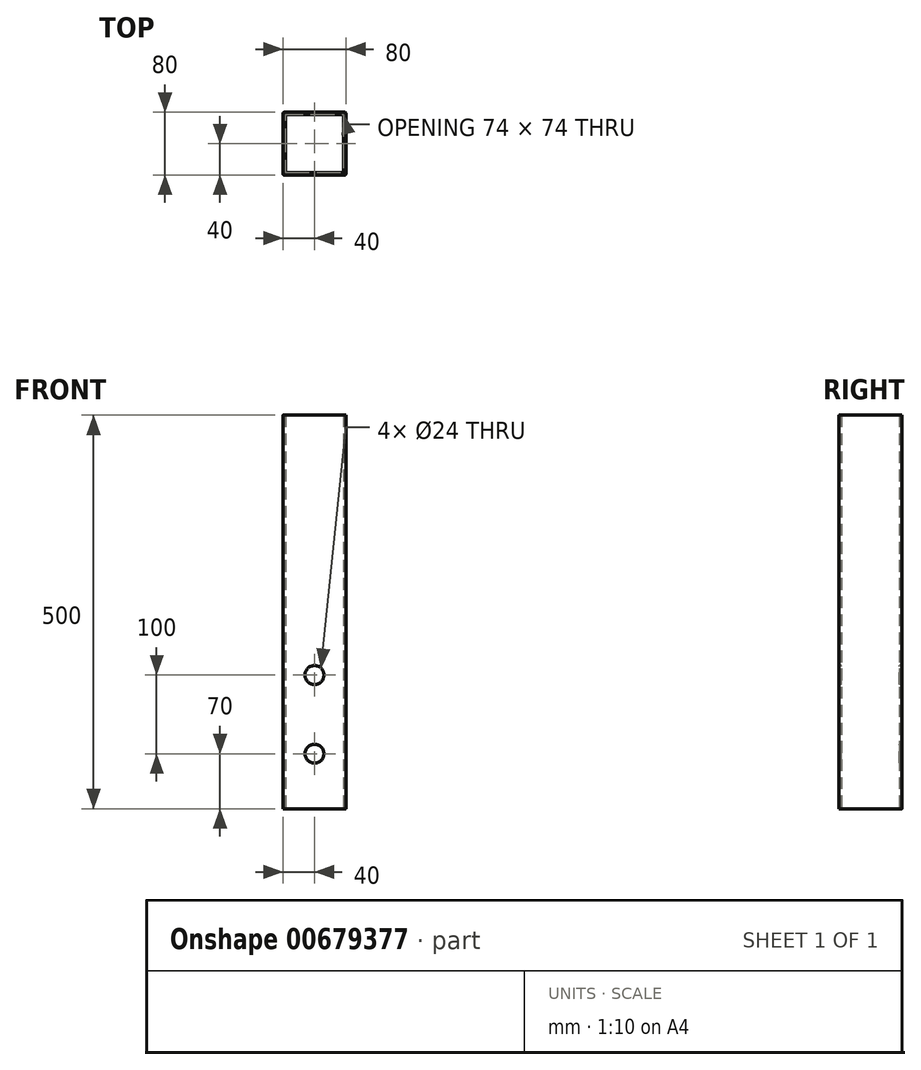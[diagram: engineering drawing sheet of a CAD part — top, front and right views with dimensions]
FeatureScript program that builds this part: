
annotation { "Feature Type Name" : "Feature", "Feature Type Description" : "" }
export const myFeature = defineFeature(function(context is Context, id is Id, definition is map)
    precondition{}
    {
        {
            var Q0;
            Q0=qCreatedBy(makeId("Top.planeOp"),FACE);
            var sketch = newSketch(context, id + "F0", { "sketchPlane" : qUnion([Q0])});
            skLineSegment(sketch, "E0.bottom", {"start": v(38, -40) * mm, "end": v(-38, -40) * mm});
            skLineSegment(sketch, "E0.top", {"start": v(38, 40) * mm, "end": v(-38, 40) * mm});
            skLineSegment(sketch, "E0.left", {"start": v(40, -38) * mm, "end": v(40, 38) * mm});
            skLineSegment(sketch, "E0.right", {"start": v(-40, -38) * mm, "end": v(-40, 38) * mm});
            skPoint(sketch, "E0.middle", {"position": v(0, 0) * mm});
            skPoint(sketch, "E1.visualSharp", {"position": v(-40, 40) * mm});
            skArc(sketch, "E1.filletArc", {"start": v(-38, 40) * mm, "mid": v(-39.41, 39.41) * mm, "end": v(-40, 38) * mm});
            skPoint(sketch, "E2.visualSharp", {"position": v(-40, -40) * mm});
            skArc(sketch, "E2.filletArc", {"start": v(-40, -38) * mm, "mid": v(-39.41, -39.41) * mm, "end": v(-38, -40) * mm});
            skPoint(sketch, "E3.visualSharp", {"position": v(40, -40) * mm});
            skArc(sketch, "E3.filletArc", {"start": v(38, -40) * mm, "mid": v(39.41, -39.41) * mm, "end": v(40, -38) * mm});
            skPoint(sketch, "E4.visualSharp", {"position": v(40, 40) * mm});
            skArc(sketch, "E4.filletArc", {"start": v(40, 38) * mm, "mid": v(39.41, 39.41) * mm, "end": v(38, 40) * mm});
            skLineSegment(sketch, "E5.0", {"start": v(35, 37) * mm, "end": v(-35, 37) * mm});
            skLineSegment(sketch, "E5.1", {"start": v(37, -35) * mm, "end": v(37, 35) * mm});
            skLineSegment(sketch, "E5.2", {"start": v(35, -37) * mm, "end": v(-35, -37) * mm});
            skLineSegment(sketch, "E5.3", {"start": v(-37, -35) * mm, "end": v(-37, 35) * mm});
            skPoint(sketch, "E6.visualSharp", {"position": v(-37, 37) * mm});
            skArc(sketch, "E6.filletArc", {"start": v(-35, 37) * mm, "mid": v(-36.41, 36.41) * mm, "end": v(-37, 35) * mm});
            skPoint(sketch, "E7.visualSharp", {"position": v(37, 37) * mm});
            skArc(sketch, "E7.filletArc", {"start": v(37, 35) * mm, "mid": v(36.41, 36.41) * mm, "end": v(35, 37) * mm});
            skPoint(sketch, "E8.visualSharp", {"position": v(37, -37) * mm});
            skArc(sketch, "E8.filletArc", {"start": v(35, -37) * mm, "mid": v(36.41, -36.41) * mm, "end": v(37, -35) * mm});
            skPoint(sketch, "E9.visualSharp", {"position": v(-37, -37) * mm});
            skArc(sketch, "E9.filletArc", {"start": v(-37, -35) * mm, "mid": v(-36.41, -36.41) * mm, "end": v(-35, -37) * mm});
            skSolve(sketch);
        }
        {
            var Q0;
            Q0=makeQuery(id+"F0.imprint","IMPRINT",FACE,{"disambiguationData":[TD([[makeQuery(id+"F0.imprint","IMPRINT",EDGE,{"derivedFrom":sQuery(id+"F0.wireOp",EDGE,"E0.bottom")}),-1.0]])]});
            extrude(context, id + "F1", {"entities" : qUnion([Q0]), "depth" : 500 * mm, "offsetDistance" : 25 * mm});
        }
        {
            var Q0;
            Q0=makeQuery(id+"F1.opExtrude","SWEPT_FACE",FACE,{"disambiguationData":[OSD([sQuery(id+"F0.wireOp",EDGE,"E0.bottom")])]});
            cPlane(context, id + "F2", {"entities" : qUnion([Q0]), "cplaneType" : CPlaneType.OFFSET, "offset" : 0 * mm, "width" : 150 * mm, "height" : 150 * mm});
        }
        {
            var Q0;
            Q0=qCreatedBy(id+"F2.planeOp",FACE);
            var sketch = newSketch(context, id + "F3", { "sketchPlane" : qUnion([Q0])});
            skPoint(sketch, "E10", {"position": v(0, 70) * mm});
            skPoint(sketch, "E11", {"position": v(0, 170) * mm});
            skSolve(sketch);
        }
        {
            var Q0;
            Q0=sQuery(id+"F3.wireOp",VERTEX,"E11");
            var Q1;
            Q1=sQuery(id+"F3.wireOp",VERTEX,"E10");
            var Q2;
            Q2=makeQuery(id+"F1.opExtrude","SWEPT_BODY",BODY,{"disambiguationData":[OSD([sQuery(id+"F0.wireOp",EDGE,"E0.bottom"),sQuery(id+"F0.wireOp",EDGE,"E0.top"),sQuery(id+"F0.wireOp",EDGE,"E0.left"),sQuery(id+"F0.wireOp",EDGE,"E0.right"),sQuery(id+"F0.wireOp",EDGE,"E1.filletArc"),sQuery(id+"F0.wireOp",EDGE,"E2.filletArc"),sQuery(id+"F0.wireOp",EDGE,"E3.filletArc"),sQuery(id+"F0.wireOp",EDGE,"E4.filletArc"),sQuery(id+"F0.wireOp",EDGE,"E5.0"),sQuery(id+"F0.wireOp",EDGE,"E5.1"),sQuery(id+"F0.wireOp",EDGE,"E5.2"),sQuery(id+"F0.wireOp",EDGE,"E5.3"),sQuery(id+"F0.wireOp",EDGE,"E6.filletArc"),sQuery(id+"F0.wireOp",EDGE,"E7.filletArc"),sQuery(id+"F0.wireOp",EDGE,"E8.filletArc"),sQuery(id+"F0.wireOp",EDGE,"E9.filletArc")])]});
            hole(context, id + "F4", {"style" : HoleStyle.SIMPLE, "endStyle" : HoleEndStyle.THROUGH, "holeDiameter" : 24 * mm, "majorDiameter" : 5 * mm, "isTappedThrough" : true, "tappedDepth" : 12 * mm, "tapClearance" : 3, "startFromSketch" : true, "locations" : qUnion([Q0, Q1]), "scope" : qUnion([Q2])});
        }
    });
